# Revit family: IS_Connect_E7736_BIM_DE
name_source: partatom
category: Plumbing Fixtures
revit_build: Autodesk Revit MEP 2016 (Build: 20161004_0715(x64)
units: mm (PartAtom-declared; Revit-internal decimal feet)

## family parameters
Always vertical = No
Cut with Voids When Loaded = No
OmniClass Number = 23.45.05.14.14
OmniClass Title = Sinks/Lavatories
Part Type = Normal
Room Calculation Point = No
Round Connector Dimension = Use Diameter
Shared = No
Work Plane-Based = No

## types (1)
- E773601 CONNECT CUBE washbasin 700x460mm, 1 taphole, with overflow
    Accessories = www.idealstandard.de\ersatzteile
    Assembly Code = C1030200
    AssetType = Fest
    BIMobject category = Basins
    BOSUseNativeGeometries = 1
    BarCode = 5017830389255
    Brand = Ideal Standard
    Brand url = http://www.idealstandard.de
    CodePerformance = DIN EN 14688 CL 10, DIN EN 31
    Color = White
    Cost = 0 $
    CurrencyUnit = €
    CurrentRevision = 1
    Date of publishing = 15/09/2017
    Description = E773601 CONNECT CUBE washbasin 700x460mm, 1 taphole, with overflow
    DrainSize = 0 mm  [stored 0 ft]
    DurationUnit = Jahr
    EAN code = https://5017830389255
    Edition number = 1
    ExpectedLife = 25
    Features = CONNECT CUBE washbasin 700x460mm, 1 taphole, with overflow
    Finish = White
    IFC Classification = Sanitary Terminal
    Installation instructions = http://www.idealstandard.de
    InstallationInstructions = www.idealstandard.de\produkte
    MainColor = White
    Manufacturer = www.idealstandard.de\produkte
    Manufacturer name = Ideal Standard
    ManufacturerURL = http://www.idealstandard.de
    Material = Vitreous china
    Material main = Vitreous china
    Model = E773601
    ModelNumber = E773601
    ModelReference = E773601 CONNECT CUBE washbasin 700x460mm, 1 taphole, with overflow
    NettWeight = 22 kg
    Nominal height = 174
    Nominal width = 700
    NominalDepth = 460 mm
    NominalHeight = 174 mm  [stored 0.570866 ft]
    NominalLength = 460 mm
    NominalWidth = 700 mm  [stored 2.29659 ft]
    Product Guid = daf9861d-738e-4964-87c3-393c1ae769c7
    Product SKU = E7736
    Product data url = https://bimobject.com
    Product family = Sanitary
    Product group = Wash basin systems
    Product name = Connect Cube Lavabo Da 70 1F Beu
    Product url = http://www.idealstandard.de
    ProductInformation = www.idealstandard.de\produkte
    QR code = http://bimobject.com
    Shape = Sculptured
    Size = 700x460x174 mm
    Space = Intern
    SpareParts = www.idealstandard.de/ersatzteile
    Technical description = http://www.idealstandard.de
    URL = http://www.idealstandard.de
    Uniclass 2.0 Code = SS-35-65-70-94
    Uniclass 2.0 Description = Wash Basin Systems
    Uniclass 2015 Code = Ss_40_15_75_94
    Uniclass 2015 Name = Wash basin systems
    Uniclass2015Code = Pr_40_20_96_96
    Uniclass2015Title = Wall-hung wash basins
    Uniclass2015Version = Products v1.1
    Version = 1
    VolumeUnits = Litres
    Weight Net (Kg) = 22

note: [stored X ft] marks values corroborated as IEEE doubles in the binary element streams (Revit-internal decimal feet)

## geometry (parser evidence)
native form markers: Blend x4, Sweep x1
no freeform markers — native parametric forms only
